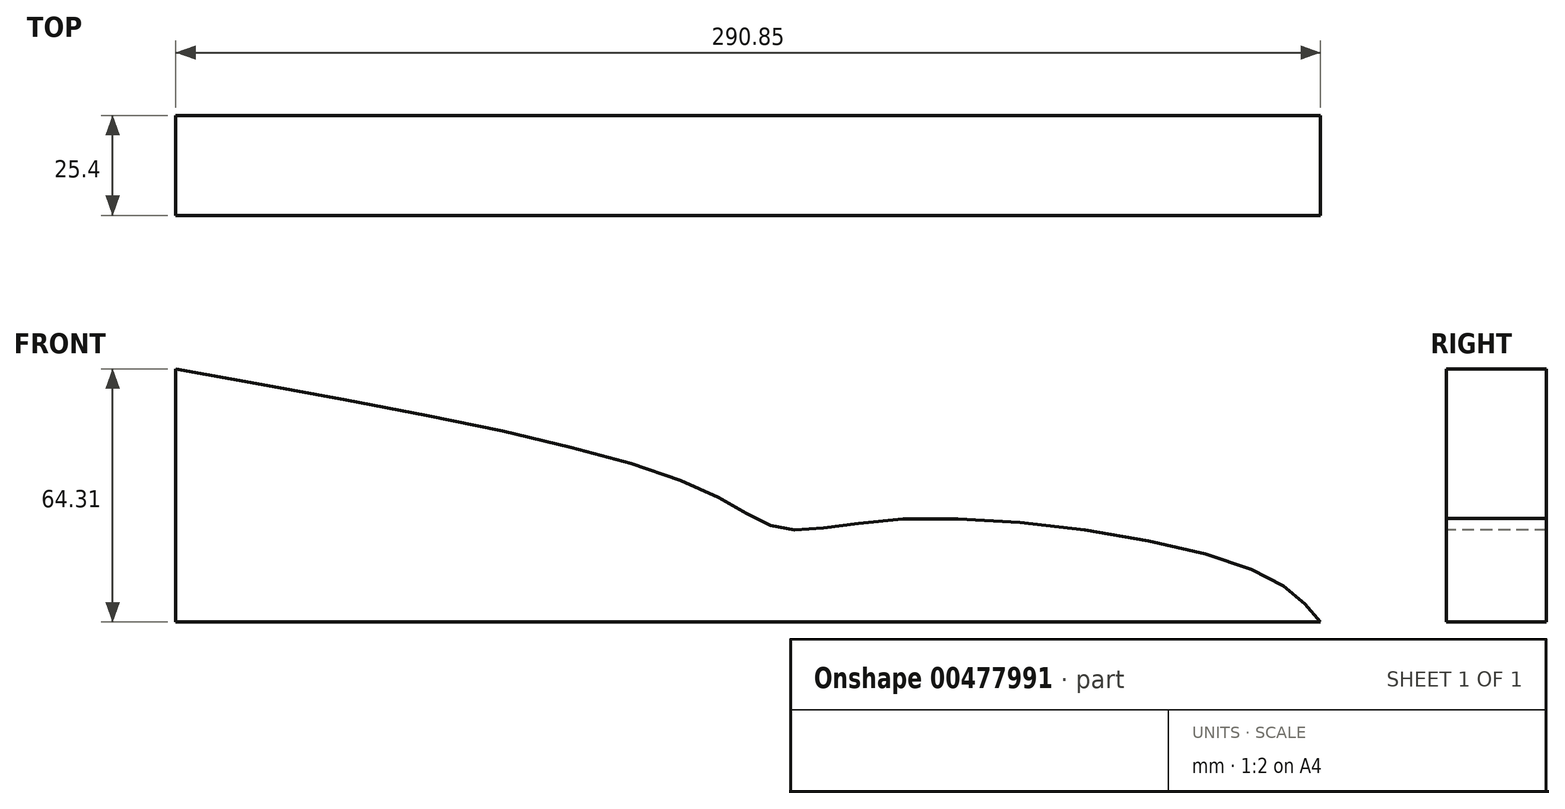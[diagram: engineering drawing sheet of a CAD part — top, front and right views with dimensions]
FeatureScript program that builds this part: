
annotation { "Feature Type Name" : "Feature", "Feature Type Description" : "" }
export const myFeature = defineFeature(function(context is Context, id is Id, definition is map)
    precondition{}
    {
        {
            var Q0;
            Q0=qCreatedBy(makeId("Front.planeOp"),FACE);
            var sketch = newSketch(context, id + "F0", { "sketchPlane" : qUnion([Q0])});
            skLineSegment(sketch, "E0.bottom", {"start": v(-147, 66.51) * mm, "end": v(143.85, 66.51) * mm});
            skLineSegment(sketch, "E0.top", {"start": v(-147, 2.2) * mm, "end": v(143.85, 2.2) * mm});
            skLineSegment(sketch, "E0.left", {"start": v(-147, 66.51) * mm, "end": v(-147, 2.2) * mm});
            skLineSegment(sketch, "E0.right", {"start": v(143.85, 66.51) * mm, "end": v(143.85, 2.2) * mm});
            skFitSpline(sketch, "E1", {"points": [v(-147, 66.51) * mm, v(-14.63, 36.48) * mm, v(7.09, 25.93) * mm, v(38.74, 28.41) * mm, v(126.88, 15.38) * mm, v(143.85, 2.2) * mm], "startDerivative": vector(504.11, -89.84) * mm, "endDerivative": vector(87.8, -107.35) * mm});
            skSolve(sketch);
        }
        {
            var Q0;
            Q0=makeQuery(id+"F0.imprint","IMPRINT",FACE,{"disambiguationData":[TD([[makeQuery(id+"F0.imprint","IMPRINT",EDGE,{"derivedFrom":sQuery(id+"F0.wireOp",EDGE,"E0.top")}),1.0]])]});
            extrude(context, id + "F1", {"entities" : qUnion([Q0]), "depth" : 25.4 * mm});
        }
    });
